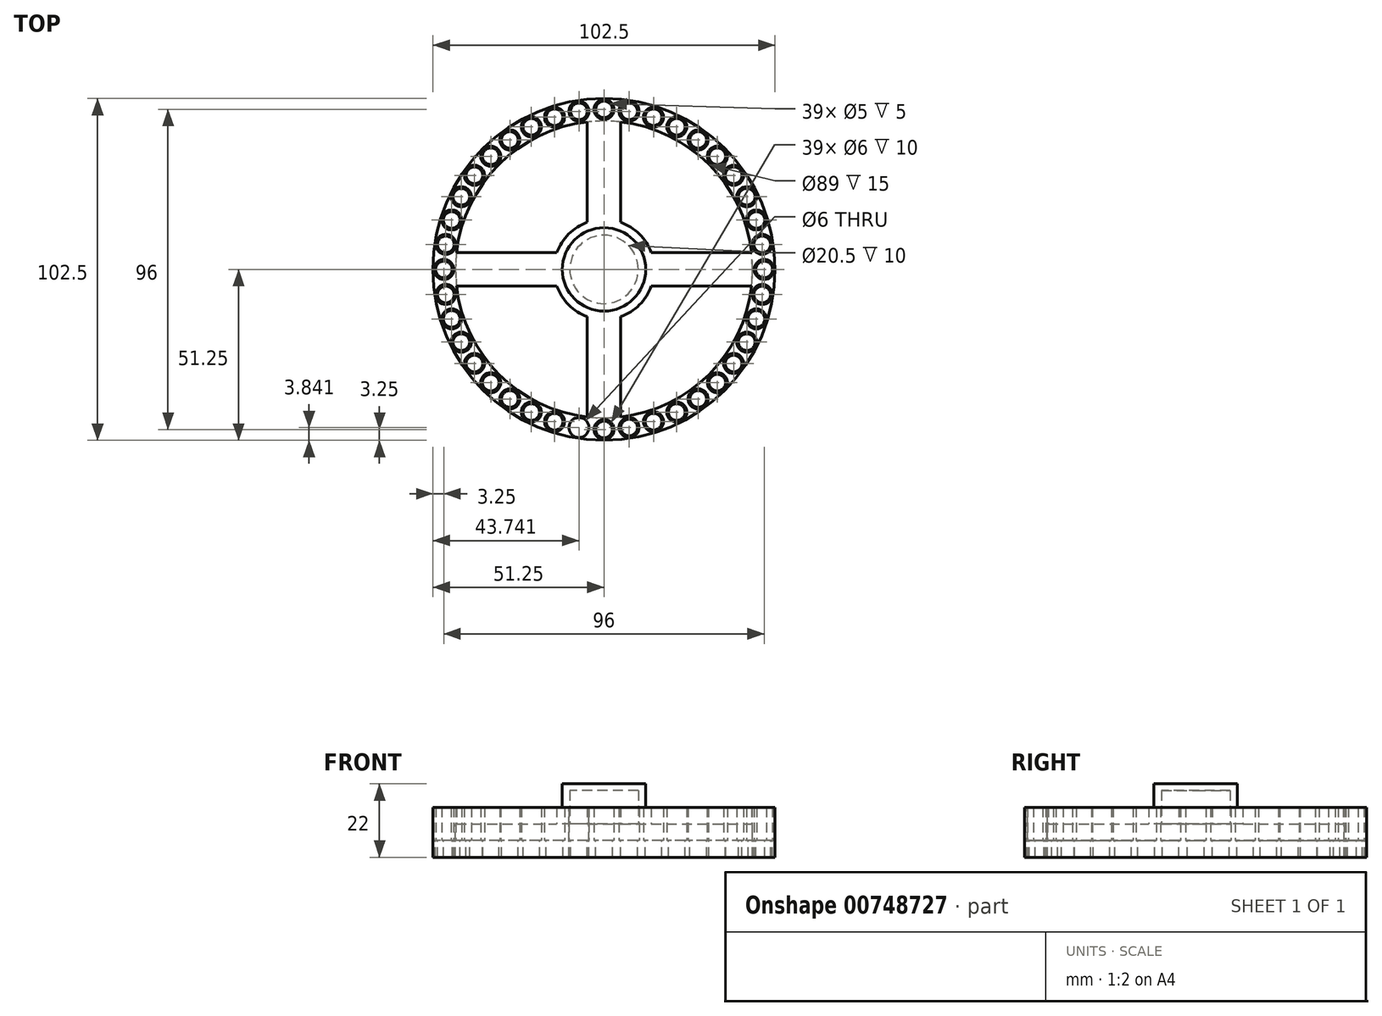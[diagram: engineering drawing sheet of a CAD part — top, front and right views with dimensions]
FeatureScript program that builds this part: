
annotation { "Feature Type Name" : "Feature", "Feature Type Description" : "" }
export const myFeature = defineFeature(function(context is Context, id is Id, definition is map)
    precondition{}
    {
        {
            var Q0;
            Q0=qCreatedBy(makeId("Top.planeOp"),FACE);
            var sketch = newSketch(context, id + "F0", { "sketchPlane" : qUnion([Q0])});
            skCircle(sketch, "E0", {"center": v(0, 0) * mm, "radius": 51.25 * mm});
            skCircle(sketch, "E1", {"center": v(0, 0) * mm, "radius": 44.5 * mm});
            skCircle(sketch, "E2", {"center": v(0, 48) * mm, "radius": 2.5 * mm});
            skCircle(sketch, "E3.1.0", {"center": v(-7.5, 47.4) * mm, "radius": 2.5 * mm});
            skCircle(sketch, "E3.2.0", {"center": v(-14.83, 45.65) * mm, "radius": 2.5 * mm});
            skCircle(sketch, "E3.3.0", {"center": v(-21.8, 42.77) * mm, "radius": 2.5 * mm});
            skCircle(sketch, "E3.4.0", {"center": v(-28.21, 38.83) * mm, "radius": 2.5 * mm});
            skCircle(sketch, "E3.5.0", {"center": v(-33.94, 33.94) * mm, "radius": 2.5 * mm});
            skCircle(sketch, "E3.6.0", {"center": v(-38.83, 28.21) * mm, "radius": 2.5 * mm});
            skCircle(sketch, "E3.7.0", {"center": v(-42.77, 21.8) * mm, "radius": 2.5 * mm});
            skCircle(sketch, "E3.8.0", {"center": v(-45.65, 14.83) * mm, "radius": 2.5 * mm});
            skCircle(sketch, "E3.9.0", {"center": v(-47.4, 7.5) * mm, "radius": 2.5 * mm});
            skCircle(sketch, "E3.10.0", {"center": v(-48, 0) * mm, "radius": 2.5 * mm});
            skCircle(sketch, "E3.11.0", {"center": v(-47.4, -7.5) * mm, "radius": 2.5 * mm});
            skCircle(sketch, "E3.12.0", {"center": v(-45.65, -14.83) * mm, "radius": 2.5 * mm});
            skCircle(sketch, "E3.13.0", {"center": v(-42.77, -21.8) * mm, "radius": 2.5 * mm});
            skCircle(sketch, "E3.14.0", {"center": v(-38.83, -28.21) * mm, "radius": 2.5 * mm});
            skCircle(sketch, "E3.15.0", {"center": v(-33.94, -33.94) * mm, "radius": 2.5 * mm});
            skCircle(sketch, "E3.16.0", {"center": v(-28.21, -38.83) * mm, "radius": 2.5 * mm});
            skCircle(sketch, "E3.17.0", {"center": v(-21.8, -42.77) * mm, "radius": 2.5 * mm});
            skCircle(sketch, "E3.18.0", {"center": v(-14.83, -45.65) * mm, "radius": 2.5 * mm});
            skCircle(sketch, "E3.19.0", {"center": v(-7.5, -47.4) * mm, "radius": 2.5 * mm});
            skCircle(sketch, "E3.20.0", {"center": v(0, -48) * mm, "radius": 2.5 * mm});
            skCircle(sketch, "E3.21.0", {"center": v(7.5, -47.4) * mm, "radius": 2.5 * mm});
            skCircle(sketch, "E3.22.0", {"center": v(14.83, -45.65) * mm, "radius": 2.5 * mm});
            skCircle(sketch, "E3.23.0", {"center": v(21.8, -42.77) * mm, "radius": 2.5 * mm});
            skCircle(sketch, "E3.24.0", {"center": v(28.21, -38.83) * mm, "radius": 2.5 * mm});
            skCircle(sketch, "E3.25.0", {"center": v(33.94, -33.94) * mm, "radius": 2.5 * mm});
            skCircle(sketch, "E3.26.0", {"center": v(38.83, -28.21) * mm, "radius": 2.5 * mm});
            skCircle(sketch, "E3.27.0", {"center": v(42.77, -21.8) * mm, "radius": 2.5 * mm});
            skCircle(sketch, "E3.28.0", {"center": v(45.65, -14.83) * mm, "radius": 2.5 * mm});
            skCircle(sketch, "E3.29.0", {"center": v(47.4, -7.5) * mm, "radius": 2.5 * mm});
            skCircle(sketch, "E3.30.0", {"center": v(48, 0) * mm, "radius": 2.5 * mm});
            skCircle(sketch, "E3.31.0", {"center": v(47.4, 7.5) * mm, "radius": 2.5 * mm});
            skCircle(sketch, "E3.32.0", {"center": v(45.65, 14.83) * mm, "radius": 2.5 * mm});
            skCircle(sketch, "E3.33.0", {"center": v(42.77, 21.8) * mm, "radius": 2.5 * mm});
            skCircle(sketch, "E3.34.0", {"center": v(38.83, 28.21) * mm, "radius": 2.5 * mm});
            skCircle(sketch, "E3.35.0", {"center": v(33.94, 33.94) * mm, "radius": 2.5 * mm});
            skCircle(sketch, "E3.36.0", {"center": v(28.21, 38.83) * mm, "radius": 2.5 * mm});
            skCircle(sketch, "E3.37.0", {"center": v(21.8, 42.77) * mm, "radius": 2.5 * mm});
            skCircle(sketch, "E3.38.0", {"center": v(14.83, 45.65) * mm, "radius": 2.5 * mm});
            skCircle(sketch, "E3.39.0", {"center": v(7.5, 47.4) * mm, "radius": 2.5 * mm});
            skLineSegment(sketch, "E4.left", {"start": v(5, -44.22) * mm, "end": v(5, -14.14) * mm});
            skLineSegment(sketch, "E4.right", {"start": v(-5, -44.22) * mm, "end": v(-5, -14.14) * mm});
            skLineSegment(sketch, "E5.bottom", {"start": v(-44.22, -5) * mm, "end": v(-14.14, -5) * mm});
            skLineSegment(sketch, "E5.top", {"start": v(-44.22, 5) * mm, "end": v(-14.14, 5) * mm});
            skCircle(sketch, "E6", {"center": v(0, 0) * mm, "radius": 15 * mm});
            skPoint(sketch, "E5.left.end.orphan", {"position": v(-45, 5) * mm});
            skPoint(sketch, "E5.left.start.orphan", {"position": v(-45, -5) * mm});
            skLineSegment(sketch, "E7.trimOffspring", {"start": v(14.14, 5) * mm, "end": v(44.22, 5) * mm});
            skLineSegment(sketch, "E8.trimOffspring", {"start": v(-5, 14.14) * mm, "end": v(-5, 44.22) * mm});
            skLineSegment(sketch, "E9.trimOffspring", {"start": v(5, 14.14) * mm, "end": v(5, 44.22) * mm});
            skLineSegment(sketch, "E10.trimOffspring", {"start": v(14.14, -5) * mm, "end": v(44.22, -5) * mm});
            skPoint(sketch, "E11.orphan", {"position": v(-5, -45) * mm});
            skPoint(sketch, "E12.orphan", {"position": v(5, -45) * mm});
            skPoint(sketch, "E13.orphan", {"position": v(45, 5) * mm});
            skPoint(sketch, "E14.orphan", {"position": v(45, -5) * mm});
            skPoint(sketch, "E4.top.start.orphan", {"position": v(5, 45) * mm});
            skPoint(sketch, "E15.orphan", {"position": v(-5, 45) * mm});
            skCircle(sketch, "E16", {"center": v(0, 48) * mm, "radius": 3 * mm});
            skCircle(sketch, "E17.1.0", {"center": v(-7.5, 47.4) * mm, "radius": 3 * mm});
            skCircle(sketch, "E17.2.0", {"center": v(-14.83, 45.65) * mm, "radius": 3 * mm});
            skCircle(sketch, "E18.1.3.0", {"center": v(-21.8, 42.77) * mm, "radius": 3 * mm});
            skCircle(sketch, "E18.1.4.0", {"center": v(-28.21, 38.83) * mm, "radius": 3 * mm});
            skCircle(sketch, "E18.1.5.0", {"center": v(-33.94, 33.94) * mm, "radius": 3 * mm});
            skCircle(sketch, "E18.1.6.0", {"center": v(-38.83, 28.21) * mm, "radius": 3 * mm});
            skCircle(sketch, "E18.1.7.0", {"center": v(-42.77, 21.8) * mm, "radius": 3 * mm});
            skCircle(sketch, "E18.1.8.0", {"center": v(-45.65, 14.83) * mm, "radius": 3 * mm});
            skCircle(sketch, "E18.1.9.0", {"center": v(-47.4, 7.5) * mm, "radius": 3 * mm});
            skCircle(sketch, "E18.1.10.0", {"center": v(-48, 0) * mm, "radius": 3 * mm});
            skCircle(sketch, "E18.1.11.0", {"center": v(-47.4, -7.5) * mm, "radius": 3 * mm});
            skCircle(sketch, "E18.1.12.0", {"center": v(-45.65, -14.83) * mm, "radius": 3 * mm});
            skCircle(sketch, "E18.1.13.0", {"center": v(-42.77, -21.8) * mm, "radius": 3 * mm});
            skCircle(sketch, "E18.1.14.0", {"center": v(-38.83, -28.21) * mm, "radius": 3 * mm});
            skCircle(sketch, "E18.1.15.0", {"center": v(-33.94, -33.94) * mm, "radius": 3 * mm});
            skCircle(sketch, "E18.1.16.0", {"center": v(-28.21, -38.83) * mm, "radius": 3 * mm});
            skCircle(sketch, "E18.1.17.0", {"center": v(-21.8, -42.77) * mm, "radius": 3 * mm});
            skCircle(sketch, "E18.1.18.0", {"center": v(-14.83, -45.65) * mm, "radius": 3 * mm});
            skCircle(sketch, "E18.1.19.0", {"center": v(-7.5, -47.4) * mm, "radius": 3 * mm});
            skCircle(sketch, "E18.1.20.0", {"center": v(0, -48) * mm, "radius": 3 * mm});
            skCircle(sketch, "E18.1.21.0", {"center": v(7.5, -47.4) * mm, "radius": 3 * mm});
            skCircle(sketch, "E18.1.22.0", {"center": v(14.83, -45.65) * mm, "radius": 3 * mm});
            skCircle(sketch, "E18.1.23.0", {"center": v(21.8, -42.77) * mm, "radius": 3 * mm});
            skCircle(sketch, "E18.1.24.0", {"center": v(28.21, -38.83) * mm, "radius": 3 * mm});
            skCircle(sketch, "E18.1.25.0", {"center": v(33.94, -33.94) * mm, "radius": 3 * mm});
            skCircle(sketch, "E18.1.26.0", {"center": v(38.83, -28.21) * mm, "radius": 3 * mm});
            skCircle(sketch, "E18.1.27.0", {"center": v(42.77, -21.8) * mm, "radius": 3 * mm});
            skCircle(sketch, "E18.1.28.0", {"center": v(45.65, -14.83) * mm, "radius": 3 * mm});
            skCircle(sketch, "E18.1.29.0", {"center": v(47.4, -7.5) * mm, "radius": 3 * mm});
            skCircle(sketch, "E18.1.30.0", {"center": v(48, 0) * mm, "radius": 3 * mm});
            skCircle(sketch, "E18.1.31.0", {"center": v(47.4, 7.5) * mm, "radius": 3 * mm});
            skCircle(sketch, "E18.1.32.0", {"center": v(45.65, 14.83) * mm, "radius": 3 * mm});
            skCircle(sketch, "E18.1.33.0", {"center": v(42.77, 21.8) * mm, "radius": 3 * mm});
            skCircle(sketch, "E18.1.34.0", {"center": v(38.83, 28.21) * mm, "radius": 3 * mm});
            skCircle(sketch, "E18.1.35.0", {"center": v(33.94, 33.94) * mm, "radius": 3 * mm});
            skCircle(sketch, "E18.1.36.0", {"center": v(28.21, 38.83) * mm, "radius": 3 * mm});
            skCircle(sketch, "E18.1.37.0", {"center": v(21.8, 42.77) * mm, "radius": 3 * mm});
            skCircle(sketch, "E18.1.38.0", {"center": v(14.83, 45.65) * mm, "radius": 3 * mm});
            skCircle(sketch, "E18.1.39.0", {"center": v(7.5, 47.4) * mm, "radius": 3 * mm});
            skSolve(sketch);
        }
        {
            var Q0;
            Q0=makeQuery(id+"F0.imprint","IMPRINT",FACE,{"disambiguationData":[TD([[makeQuery(id+"F0.imprint","IMPRINT",EDGE,{"derivedFrom":sQuery(id+"F0.wireOp",EDGE,"E2")}),-1.0]])]});
            var Q1;
            Q1=makeQuery(id+"F0.imprint","IMPRINT",FACE,{"disambiguationData":[TD([[makeQuery(id+"F0.imprint","IMPRINT",EDGE,{"derivedFrom":sQuery(id+"F0.wireOp",EDGE,"E3.37.0")}),-1.0]])]});
            var Q2;
            Q2=makeQuery(id+"F0.imprint","IMPRINT",FACE,{"disambiguationData":[TD([[makeQuery(id+"F0.imprint","IMPRINT",EDGE,{"derivedFrom":sQuery(id+"F0.wireOp",EDGE,"E3.38.0")}),-1.0]])]});
            var Q3;
            Q3=makeQuery(id+"F0.imprint","IMPRINT",FACE,{"disambiguationData":[TD([[makeQuery(id+"F0.imprint","IMPRINT",EDGE,{"derivedFrom":sQuery(id+"F0.wireOp",EDGE,"E3.39.0")}),-1.0]])]});
            var Q4;
            Q4=makeQuery(id+"F0.imprint","IMPRINT",FACE,{"disambiguationData":[TD([[makeQuery(id+"F0.imprint","IMPRINT",EDGE,{"derivedFrom":sQuery(id+"F0.wireOp",EDGE,"E3.35.0")}),-1.0]])]});
            var Q5;
            Q5=makeQuery(id+"F0.imprint","IMPRINT",FACE,{"disambiguationData":[TD([[makeQuery(id+"F0.imprint","IMPRINT",EDGE,{"derivedFrom":sQuery(id+"F0.wireOp",EDGE,"E3.34.0")}),-1.0]])]});
            var Q6;
            Q6=makeQuery(id+"F0.imprint","IMPRINT",FACE,{"disambiguationData":[TD([[makeQuery(id+"F0.imprint","IMPRINT",EDGE,{"derivedFrom":sQuery(id+"F0.wireOp",EDGE,"E3.33.0")}),-1.0]])]});
            var Q7;
            Q7=makeQuery(id+"F0.imprint","IMPRINT",FACE,{"disambiguationData":[TD([[makeQuery(id+"F0.imprint","IMPRINT",EDGE,{"derivedFrom":sQuery(id+"F0.wireOp",EDGE,"E3.32.0")}),-1.0]])]});
            var Q8;
            Q8=makeQuery(id+"F0.imprint","IMPRINT",FACE,{"disambiguationData":[TD([[makeQuery(id+"F0.imprint","IMPRINT",EDGE,{"derivedFrom":sQuery(id+"F0.wireOp",EDGE,"E3.31.0")}),-1.0]])]});
            var Q9;
            Q9=makeQuery(id+"F0.imprint","IMPRINT",FACE,{"disambiguationData":[TD([[makeQuery(id+"F0.imprint","IMPRINT",EDGE,{"derivedFrom":sQuery(id+"F0.wireOp",EDGE,"E3.30.0")}),-1.0]])]});
            var Q10;
            Q10=makeQuery(id+"F0.imprint","IMPRINT",FACE,{"disambiguationData":[TD([[makeQuery(id+"F0.imprint","IMPRINT",EDGE,{"derivedFrom":sQuery(id+"F0.wireOp",EDGE,"E3.29.0")}),-1.0]])]});
            var Q11;
            Q11=makeQuery(id+"F0.imprint","IMPRINT",FACE,{"disambiguationData":[TD([[makeQuery(id+"F0.imprint","IMPRINT",EDGE,{"derivedFrom":sQuery(id+"F0.wireOp",EDGE,"E3.26.0")}),-1.0]])]});
            var Q12;
            Q12=makeQuery(id+"F0.imprint","IMPRINT",FACE,{"disambiguationData":[TD([[makeQuery(id+"F0.imprint","IMPRINT",EDGE,{"derivedFrom":sQuery(id+"F0.wireOp",EDGE,"E3.24.0")}),-1.0]])]});
            var Q13;
            Q13=makeQuery(id+"F0.imprint","IMPRINT",FACE,{"disambiguationData":[TD([[makeQuery(id+"F0.imprint","IMPRINT",EDGE,{"derivedFrom":sQuery(id+"F0.wireOp",EDGE,"E3.23.0")}),-1.0]])]});
            var Q14;
            Q14=makeQuery(id+"F0.imprint","IMPRINT",FACE,{"disambiguationData":[TD([[makeQuery(id+"F0.imprint","IMPRINT",EDGE,{"derivedFrom":sQuery(id+"F0.wireOp",EDGE,"E3.22.0")}),-1.0]])]});
            var Q15;
            Q15=makeQuery(id+"F0.imprint","IMPRINT",FACE,{"disambiguationData":[TD([[makeQuery(id+"F0.imprint","IMPRINT",EDGE,{"derivedFrom":sQuery(id+"F0.wireOp",EDGE,"E3.20.0")}),-1.0]])]});
            var Q16;
            Q16=makeQuery(id+"F0.imprint","IMPRINT",FACE,{"disambiguationData":[TD([[makeQuery(id+"F0.imprint","IMPRINT",EDGE,{"derivedFrom":sQuery(id+"F0.wireOp",EDGE,"E3.21.0")}),-1.0]])]});
            var Q17;
            Q17=makeQuery(id+"F0.imprint","IMPRINT",FACE,{"disambiguationData":[TD([[makeQuery(id+"F0.imprint","IMPRINT",EDGE,{"derivedFrom":sQuery(id+"F0.wireOp",EDGE,"E3.18.0")}),-1.0]])]});
            var Q18;
            Q18=makeQuery(id+"F0.imprint","IMPRINT",FACE,{"disambiguationData":[TD([[makeQuery(id+"F0.imprint","IMPRINT",EDGE,{"derivedFrom":sQuery(id+"F0.wireOp",EDGE,"E3.17.0")}),-1.0]])]});
            var Q19;
            Q19=makeQuery(id+"F0.imprint","IMPRINT",FACE,{"disambiguationData":[TD([[makeQuery(id+"F0.imprint","IMPRINT",EDGE,{"derivedFrom":sQuery(id+"F0.wireOp",EDGE,"E3.16.0")}),-1.0]])]});
            var Q20;
            Q20=makeQuery(id+"F0.imprint","IMPRINT",FACE,{"disambiguationData":[TD([[makeQuery(id+"F0.imprint","IMPRINT",EDGE,{"derivedFrom":sQuery(id+"F0.wireOp",EDGE,"E3.15.0")}),-1.0]])]});
            var Q21;
            Q21=makeQuery(id+"F0.imprint","IMPRINT",FACE,{"disambiguationData":[TD([[makeQuery(id+"F0.imprint","IMPRINT",EDGE,{"derivedFrom":sQuery(id+"F0.wireOp",EDGE,"E3.14.0")}),-1.0]])]});
            var Q22;
            Q22=makeQuery(id+"F0.imprint","IMPRINT",FACE,{"disambiguationData":[TD([[makeQuery(id+"F0.imprint","IMPRINT",EDGE,{"derivedFrom":sQuery(id+"F0.wireOp",EDGE,"E3.13.0")}),-1.0]])]});
            var Q23;
            Q23=makeQuery(id+"F0.imprint","IMPRINT",FACE,{"disambiguationData":[TD([[makeQuery(id+"F0.imprint","IMPRINT",EDGE,{"derivedFrom":sQuery(id+"F0.wireOp",EDGE,"E3.12.0")}),-1.0]])]});
            var Q24;
            Q24=makeQuery(id+"F0.imprint","IMPRINT",FACE,{"disambiguationData":[TD([[makeQuery(id+"F0.imprint","IMPRINT",EDGE,{"derivedFrom":sQuery(id+"F0.wireOp",EDGE,"E3.11.0")}),-1.0]])]});
            var Q25;
            Q25=makeQuery(id+"F0.imprint","IMPRINT",FACE,{"disambiguationData":[TD([[makeQuery(id+"F0.imprint","IMPRINT",EDGE,{"derivedFrom":sQuery(id+"F0.wireOp",EDGE,"E3.9.0")}),-1.0]])]});
            var Q26;
            Q26=makeQuery(id+"F0.imprint","IMPRINT",FACE,{"disambiguationData":[TD([[makeQuery(id+"F0.imprint","IMPRINT",EDGE,{"derivedFrom":sQuery(id+"F0.wireOp",EDGE,"E3.7.0")}),-1.0]])]});
            var Q27;
            Q27=makeQuery(id+"F0.imprint","IMPRINT",FACE,{"disambiguationData":[TD([[makeQuery(id+"F0.imprint","IMPRINT",EDGE,{"derivedFrom":sQuery(id+"F0.wireOp",EDGE,"E3.3.0")}),-1.0]])]});
            var Q28;
            Q28=makeQuery(id+"F0.imprint","IMPRINT",FACE,{"disambiguationData":[TD([[makeQuery(id+"F0.imprint","IMPRINT",EDGE,{"derivedFrom":sQuery(id+"F0.wireOp",EDGE,"E3.2.0")}),-1.0]])]});
            var Q29;
            Q29=makeQuery(id+"F0.imprint","IMPRINT",FACE,{"disambiguationData":[TD([[makeQuery(id+"F0.imprint","IMPRINT",EDGE,{"derivedFrom":sQuery(id+"F0.wireOp",EDGE,"E3.1.0")}),-1.0]])]});
            var Q30;
            Q30=makeQuery(id+"F0.imprint","IMPRINT",FACE,{"disambiguationData":[TD([[makeQuery(id+"F0.imprint","IMPRINT",EDGE,{"derivedFrom":sQuery(id+"F0.wireOp",EDGE,"E3.6.0")}),-1.0]])]});
            var Q31;
            Q31=makeQuery(id+"F0.imprint","IMPRINT",FACE,{"disambiguationData":[TD([[makeQuery(id+"F0.imprint","IMPRINT",EDGE,{"derivedFrom":sQuery(id+"F0.wireOp",EDGE,"E3.5.0")}),-1.0]])]});
            var Q32;
            Q32=makeQuery(id+"F0.imprint","IMPRINT",FACE,{"disambiguationData":[TD([[makeQuery(id+"F0.imprint","IMPRINT",EDGE,{"derivedFrom":sQuery(id+"F0.wireOp",EDGE,"E3.4.0")}),-1.0]])]});
            var Q33;
            Q33=makeQuery(id+"F0.imprint","IMPRINT",FACE,{"disambiguationData":[TD([[makeQuery(id+"F0.imprint","IMPRINT",EDGE,{"derivedFrom":sQuery(id+"F0.wireOp",EDGE,"E3.10.0")}),-1.0]])]});
            var Q34;
            Q34=makeQuery(id+"F0.imprint","IMPRINT",FACE,{"disambiguationData":[TD([[makeQuery(id+"F0.imprint","IMPRINT",EDGE,{"derivedFrom":sQuery(id+"F0.wireOp",EDGE,"E3.8.0")}),-1.0]])]});
            var Q35;
            Q35=makeQuery(id+"F0.imprint","IMPRINT",FACE,{"disambiguationData":[TD([[makeQuery(id+"F0.imprint","IMPRINT",EDGE,{"derivedFrom":sQuery(id+"F0.wireOp",EDGE,"E0")}),1.0]])]});
            var Q36;
            Q36=makeQuery(id+"F0.imprint","IMPRINT",FACE,{"disambiguationData":[TD([[makeQuery(id+"F0.imprint","IMPRINT",EDGE,{"derivedFrom":sQuery(id+"F0.wireOp",EDGE,"E3.25.0")}),-1.0]])]});
            var Q37;
            Q37=makeQuery(id+"F0.imprint","IMPRINT",FACE,{"disambiguationData":[TD([[makeQuery(id+"F0.imprint","IMPRINT",EDGE,{"derivedFrom":sQuery(id+"F0.wireOp",EDGE,"E3.28.0")}),-1.0]])]});
            var Q38;
            Q38=makeQuery(id+"F0.imprint","IMPRINT",FACE,{"disambiguationData":[TD([[makeQuery(id+"F0.imprint","IMPRINT",EDGE,{"derivedFrom":sQuery(id+"F0.wireOp",EDGE,"E3.27.0")}),-1.0]])]});
            var Q39;
            Q39=makeQuery(id+"F0.imprint","IMPRINT",FACE,{"disambiguationData":[TD([[makeQuery(id+"F0.imprint","IMPRINT",EDGE,{"derivedFrom":sQuery(id+"F0.wireOp",EDGE,"E3.36.0")}),-1.0]])]});
            extrude(context, id + "F1", {"entities" : qUnion([Q0, Q1, Q2, Q3, Q4, Q5, Q6, Q7, Q8, Q9, Q10, Q11, Q12, Q13, Q14, Q15, Q16, Q17, Q18, Q19, Q20, Q21, Q22, Q23, Q24, Q25, Q26, Q27, Q28, Q29, Q30, Q31, Q32, Q33, Q34, Q35, Q36, Q37, Q38, Q39]), "oppositeDirection" : true, "depth" : 10 * mm, "offsetDistance" : 25 * mm, "hasSecondDirection" : true, "secondDirectionOppositeDirection" : false, "secondDirectionDepth" : 5 * mm});
        }
        {
            var Q0;
            {var subQ0=sQuery(id+"F0.wireOp",EDGE,"E8.trimOffspring");Q0=makeQuery(id+"F0.imprint","IMPRINT",FACE,{"disambiguationData":[TD([[makeQuery(id+"F0.imprint","IMPRINT",EDGE,{"derivedFrom":subQ0}),-1.0]])]});}
            var Q1;
            {var subQ0=sQuery(id+"F0.wireOp",EDGE,"E6");var subQ5=makeQuery(id+"F0.imprint","INTERSECT",VERTEX,{"derivedFrom":[subQ0,sQuery(id+"F0.wireOp",EDGE,"E7.trimOffspring")]});Q1=makeQuery(id+"F0.imprint","IMPRINT",FACE,{"disambiguationData":[TD([[makeQuery(id+"F0.imprint","IMPRINT",EDGE,{"disambiguationData":[TD([[subQ5,-1.0]])],"derivedFrom":subQ0}),1.0]])]});}
            var Q2;
            {var subQ0=sQuery(id+"F0.wireOp",EDGE,"E4.left");Q2=makeQuery(id+"F0.imprint","IMPRINT",FACE,{"disambiguationData":[TD([[makeQuery(id+"F0.imprint","IMPRINT",EDGE,{"derivedFrom":subQ0}),1.0]])]});}
            var Q3;
            {var subQ0=sQuery(id+"F0.wireOp",EDGE,"E5.bottom");Q3=makeQuery(id+"F0.imprint","IMPRINT",FACE,{"disambiguationData":[TD([[makeQuery(id+"F0.imprint","IMPRINT",EDGE,{"derivedFrom":subQ0}),1.0]])]});}
            var Q4;
            {var subQ0=sQuery(id+"F0.wireOp",EDGE,"E7.trimOffspring");Q4=makeQuery(id+"F0.imprint","IMPRINT",FACE,{"disambiguationData":[TD([[makeQuery(id+"F0.imprint","IMPRINT",EDGE,{"derivedFrom":subQ0}),-1.0]])]});}
            extrude(context, id + "F2", {"entities" : qUnion([Q0, Q1, Q2, Q3, Q4]), "operationType" : NewBodyOperationType.ADD, "depth" : 5 * mm, "offsetDistance" : 25 * mm});
        }
        {
            var Q0;
            Q0=qCreatedBy(makeId("Top.planeOp"),FACE);
            var sketch = newSketch(context, id + "F3", { "sketchPlane" : qUnion([Q0])});
            skCircle(sketch, "E19", {"center": v(0, 48) * mm, "radius": 3 * mm});
            skCircle(sketch, "E20.1.0", {"center": v(-7.5, 47.4) * mm, "radius": 3 * mm});
            skCircle(sketch, "E20.2.0", {"center": v(-14.83, 45.65) * mm, "radius": 3 * mm});
            skCircle(sketch, "E20.3.0", {"center": v(-21.8, 42.77) * mm, "radius": 3 * mm});
            skCircle(sketch, "E20.4.0", {"center": v(-28.21, 38.83) * mm, "radius": 3 * mm});
            skCircle(sketch, "E20.5.0", {"center": v(-33.94, 33.94) * mm, "radius": 3 * mm});
            skCircle(sketch, "E20.6.0", {"center": v(-38.83, 28.21) * mm, "radius": 3 * mm});
            skCircle(sketch, "E20.7.0", {"center": v(-42.77, 21.8) * mm, "radius": 3 * mm});
            skCircle(sketch, "E20.8.0", {"center": v(-45.65, 14.83) * mm, "radius": 3 * mm});
            skCircle(sketch, "E20.9.0", {"center": v(-47.4, 7.5) * mm, "radius": 3 * mm});
            skCircle(sketch, "E20.10.0", {"center": v(-48, 0) * mm, "radius": 3 * mm});
            skCircle(sketch, "E20.11.0", {"center": v(-47.4, -7.5) * mm, "radius": 3 * mm});
            skCircle(sketch, "E20.12.0", {"center": v(-45.65, -14.83) * mm, "radius": 3 * mm});
            skCircle(sketch, "E20.13.0", {"center": v(-42.77, -21.8) * mm, "radius": 3 * mm});
            skCircle(sketch, "E20.14.0", {"center": v(-38.83, -28.21) * mm, "radius": 3 * mm});
            skCircle(sketch, "E20.15.0", {"center": v(-33.94, -33.94) * mm, "radius": 3 * mm});
            skCircle(sketch, "E20.16.0", {"center": v(-28.21, -38.83) * mm, "radius": 3 * mm});
            skCircle(sketch, "E20.17.0", {"center": v(-21.8, -42.77) * mm, "radius": 3 * mm});
            skCircle(sketch, "E20.18.0", {"center": v(-14.83, -45.65) * mm, "radius": 3 * mm});
            skCircle(sketch, "E20.19.0", {"center": v(-7.5, -47.4) * mm, "radius": 3 * mm});
            skCircle(sketch, "E20.20.0", {"center": v(0, -48) * mm, "radius": 3 * mm});
            skCircle(sketch, "E20.21.0", {"center": v(7.5, -47.4) * mm, "radius": 3 * mm});
            skCircle(sketch, "E20.22.0", {"center": v(14.83, -45.65) * mm, "radius": 3 * mm});
            skCircle(sketch, "E20.23.0", {"center": v(21.8, -42.77) * mm, "radius": 3 * mm});
            skCircle(sketch, "E20.24.0", {"center": v(28.21, -38.83) * mm, "radius": 3 * mm});
            skCircle(sketch, "E20.25.0", {"center": v(33.94, -33.94) * mm, "radius": 3 * mm});
            skCircle(sketch, "E20.26.0", {"center": v(38.83, -28.21) * mm, "radius": 3 * mm});
            skCircle(sketch, "E20.27.0", {"center": v(42.77, -21.8) * mm, "radius": 3 * mm});
            skCircle(sketch, "E20.28.0", {"center": v(45.65, -14.83) * mm, "radius": 3 * mm});
            skCircle(sketch, "E20.29.0", {"center": v(47.4, -7.5) * mm, "radius": 3 * mm});
            skCircle(sketch, "E20.30.0", {"center": v(48, 0) * mm, "radius": 3 * mm});
            skCircle(sketch, "E20.31.0", {"center": v(47.4, 7.5) * mm, "radius": 3 * mm});
            skCircle(sketch, "E20.32.0", {"center": v(45.65, 14.83) * mm, "radius": 3 * mm});
            skCircle(sketch, "E20.33.0", {"center": v(42.77, 21.8) * mm, "radius": 3 * mm});
            skCircle(sketch, "E20.34.0", {"center": v(38.83, 28.21) * mm, "radius": 3 * mm});
            skCircle(sketch, "E20.35.0", {"center": v(33.94, 33.94) * mm, "radius": 3 * mm});
            skCircle(sketch, "E20.36.0", {"center": v(28.21, 38.83) * mm, "radius": 3 * mm});
            skCircle(sketch, "E20.37.0", {"center": v(21.8, 42.77) * mm, "radius": 3 * mm});
            skCircle(sketch, "E20.38.0", {"center": v(14.83, 45.65) * mm, "radius": 3 * mm});
            skCircle(sketch, "E20.39.0", {"center": v(7.5, 47.4) * mm, "radius": 3 * mm});
            skPoint(sketch, "E20.center", {"position": v(0, 0) * mm});
            skSolve(sketch);
        }
        {
            var Q0;
            Q0 = qSketchRegion(id + "F3", true);
            var Q1;
            {var subQ0=sQuery(id+"F0.wireOp",EDGE,"E1");Q1=makeQuery(id+"F2.boolean.opBoolean","MERGE",FACE,{"derivedFrom":[makeQuery(id+"F1.opExtrude","CAP_FACE",FACE,{"disambiguationData":[OSD([sQuery(id+"F0.wireOp",EDGE,"E0"),subQ0,sQuery(id+"F0.wireOp",EDGE,"E2"),sQuery(id+"F0.wireOp",EDGE,"E3.1.0"),sQuery(id+"F0.wireOp",EDGE,"E3.2.0"),sQuery(id+"F0.wireOp",EDGE,"E3.3.0"),sQuery(id+"F0.wireOp",EDGE,"E3.4.0"),sQuery(id+"F0.wireOp",EDGE,"E3.5.0"),sQuery(id+"F0.wireOp",EDGE,"E3.6.0"),sQuery(id+"F0.wireOp",EDGE,"E3.7.0"),sQuery(id+"F0.wireOp",EDGE,"E3.8.0"),sQuery(id+"F0.wireOp",EDGE,"E3.9.0"),sQuery(id+"F0.wireOp",EDGE,"E3.10.0"),sQuery(id+"F0.wireOp",EDGE,"E3.11.0"),sQuery(id+"F0.wireOp",EDGE,"E3.12.0"),sQuery(id+"F0.wireOp",EDGE,"E3.13.0"),sQuery(id+"F0.wireOp",EDGE,"E3.14.0"),sQuery(id+"F0.wireOp",EDGE,"E3.15.0"),sQuery(id+"F0.wireOp",EDGE,"E3.16.0"),sQuery(id+"F0.wireOp",EDGE,"E3.17.0"),sQuery(id+"F0.wireOp",EDGE,"E3.18.0"),sQuery(id+"F0.wireOp",EDGE,"E3.20.0"),sQuery(id+"F0.wireOp",EDGE,"E3.21.0"),sQuery(id+"F0.wireOp",EDGE,"E3.22.0"),sQuery(id+"F0.wireOp",EDGE,"E3.23.0"),sQuery(id+"F0.wireOp",EDGE,"E3.24.0"),sQuery(id+"F0.wireOp",EDGE,"E3.25.0"),sQuery(id+"F0.wireOp",EDGE,"E3.26.0"),sQuery(id+"F0.wireOp",EDGE,"E3.27.0"),sQuery(id+"F0.wireOp",EDGE,"E3.28.0"),sQuery(id+"F0.wireOp",EDGE,"E3.29.0"),sQuery(id+"F0.wireOp",EDGE,"E3.30.0"),sQuery(id+"F0.wireOp",EDGE,"E3.31.0"),sQuery(id+"F0.wireOp",EDGE,"E3.32.0"),sQuery(id+"F0.wireOp",EDGE,"E3.33.0"),sQuery(id+"F0.wireOp",EDGE,"E3.34.0"),sQuery(id+"F0.wireOp",EDGE,"E3.35.0"),sQuery(id+"F0.wireOp",EDGE,"E3.36.0"),sQuery(id+"F0.wireOp",EDGE,"E3.37.0"),sQuery(id+"F0.wireOp",EDGE,"E3.38.0"),sQuery(id+"F0.wireOp",EDGE,"E3.39.0"),sQuery(id+"F0.wireOp",EDGE,"E18.1.19.0")])],"isStart":true}),makeQuery(id+"F2.opExtrude","CAP_FACE",FACE,{"disambiguationData":[OSD([subQ0,sQuery(id+"F0.wireOp",EDGE,"E4.left"),sQuery(id+"F0.wireOp",EDGE,"E4.right"),sQuery(id+"F0.wireOp",EDGE,"E5.bottom"),sQuery(id+"F0.wireOp",EDGE,"E5.top"),sQuery(id+"F0.wireOp",EDGE,"E6"),sQuery(id+"F0.wireOp",EDGE,"E7.trimOffspring"),sQuery(id+"F0.wireOp",EDGE,"E8.trimOffspring"),sQuery(id+"F0.wireOp",EDGE,"E9.trimOffspring"),sQuery(id+"F0.wireOp",EDGE,"E10.trimOffspring")])],"isStart":false})]});}
            extrude(context, id + "F4", {"entities" : qUnion([Q0]), "operationType" : NewBodyOperationType.REMOVE, "endBound" : BoundingType.UP_TO_SURFACE, "depth" : 25 * mm, "endBoundEntityFace" : qUnion([Q1]), "offsetDistance" : 25 * mm, "hasSecondDirection" : true, "secondDirectionOppositeDirection" : true, "secondDirectionDepth" : 5 * mm});
        }
        {
            var Q0;
            Q0 = qSketchRegion(id + "F0", true);
            var sketch = newSketch(context, id + "F5", { "sketchPlane" : qUnion([Q0])});
            skCircle(sketch, "E21", {"center": v(0, 0) * mm, "radius": 12.5 * mm});
            skSolve(sketch);
        }
        {
            var Q0;
            Q0 = qSketchRegion(id + "F5", true);
            extrude(context, id + "F6", {"entities" : qUnion([Q0]), "operationType" : NewBodyOperationType.ADD, "depth" : 12 * mm, "offsetDistance" : 25 * mm});
        }
        {
            var Q0;
            Q0 = qSketchRegion(id + "F0", true);
            var sketch = newSketch(context, id + "F7", { "sketchPlane" : qUnion([Q0])});
            skCircle(sketch, "E22", {"center": v(0, 0) * mm, "radius": 10.25 * mm});
            skSolve(sketch);
        }
        {
            var Q0;
            Q0 = qSketchRegion(id + "F7", true);
            extrude(context, id + "F8", {"entities" : qUnion([Q0]), "operationType" : NewBodyOperationType.REMOVE, "depth" : 10 * mm, "offsetDistance" : 25 * mm});
        }
    });
